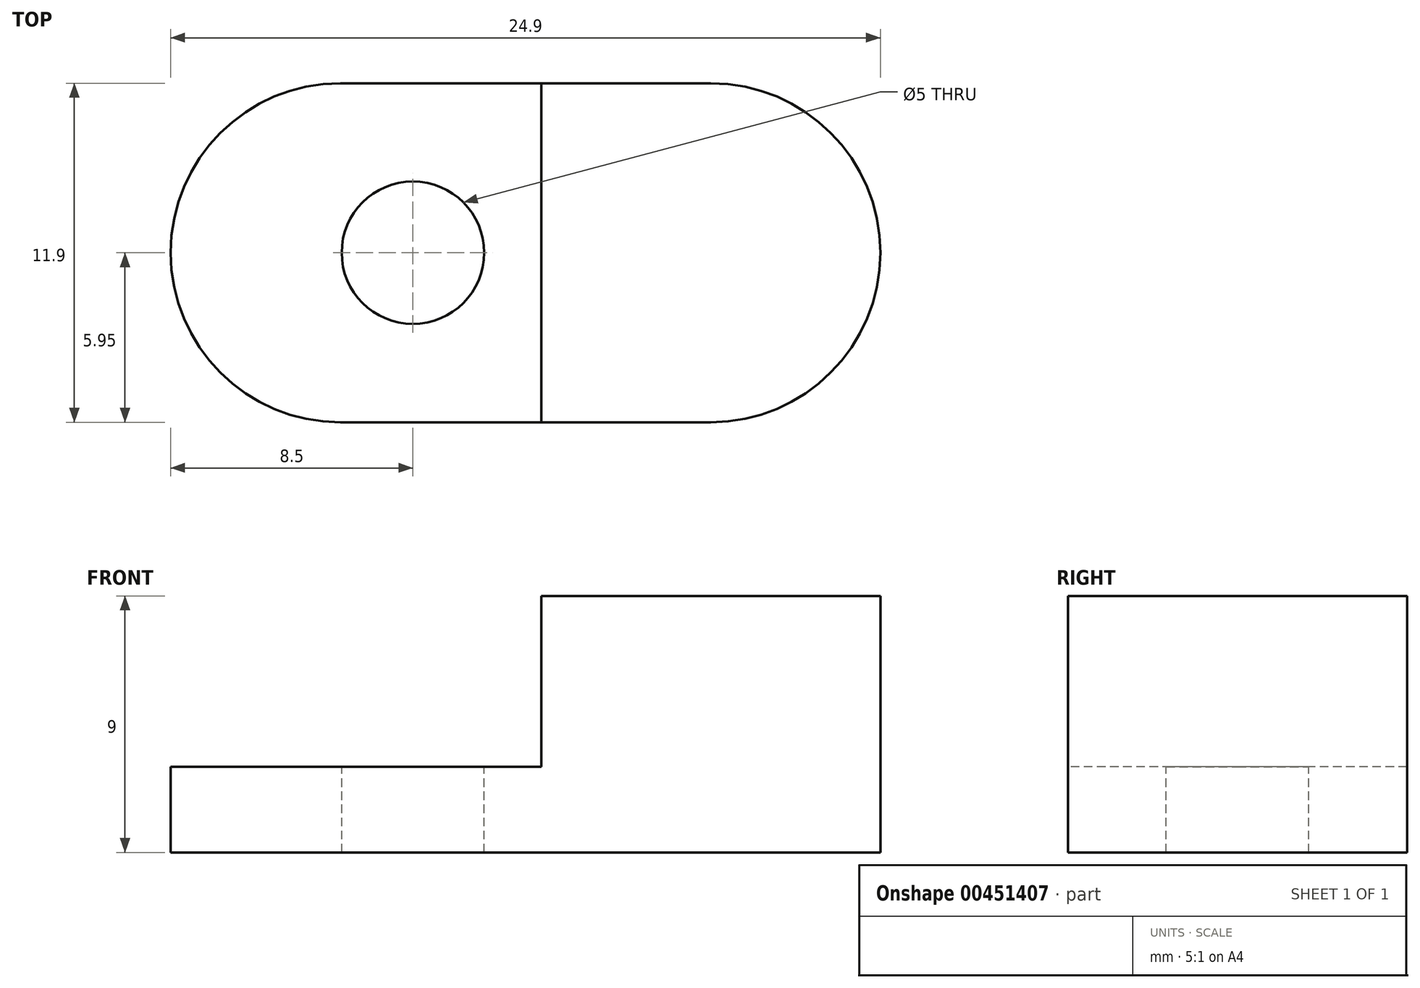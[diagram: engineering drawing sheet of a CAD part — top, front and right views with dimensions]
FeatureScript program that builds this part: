
annotation { "Feature Type Name" : "Feature", "Feature Type Description" : "" }
export const myFeature = defineFeature(function(context is Context, id is Id, definition is map)
    precondition{}
    {
        {
            var Q0;
            Q0=qCreatedBy(makeId("Top.planeOp"),FACE);
            var sketch = newSketch(context, id + "F0", { "sketchPlane" : qUnion([Q0])});
            skLineSegment(sketch, "E0.bottom", {"start": v(-6.5, -5.95) * mm, "end": v(6.5, -5.95) * mm});
            skLineSegment(sketch, "E0.top", {"start": v(-6.5, 5.95) * mm, "end": v(6.5, 5.95) * mm});
            skArc(sketch, "E1", {"start": v(-6.5, 5.95) * mm, "mid": v(-12.45, 0) * mm, "end": v(-6.5, -5.95) * mm});
            skLineSegment(sketch, "E2", {"start": v(-6.5, 8.48) * mm, "end": v(-6.5, -9.76) * mm, "construction": true});
            skArc(sketch, "E3.MirrorCS", {"start": v(6.5, 5.95) * mm, "mid": v(12.45, 0) * mm, "end": v(6.5, -5.95) * mm});
            skLineSegment(sketch, "E4", {"start": v(6.5, 7.97) * mm, "end": v(6.5, -10.02) * mm, "construction": true});
            skPoint(sketch, "E5.endSnap0", {"position": v(-12.45, 0) * mm});
            skCircle(sketch, "E6", {"center": v(-3.95, 0) * mm, "radius": 2.5 * mm});
            skLineSegment(sketch, "E7", {"start": v(-16.35, 0) * mm, "end": v(15.83, 0) * mm, "construction": true});
            skSolve(sketch);
        }
        {
            var Q0;
            Q0=makeQuery(id+"F0.imprint","IMPRINT",FACE,{"disambiguationData":[TD([[makeQuery(id+"F0.imprint","IMPRINT",EDGE,{"derivedFrom":sQuery(id+"F0.wireOp",EDGE,"E0.bottom")}),1.0]])]});
            var Q1;
            Q1=makeQuery(id+"F0.imprint","IMPRINT",FACE,{"disambiguationData":[TD([[makeQuery(id+"F0.imprint","IMPRINT",EDGE,{"derivedFrom":sQuery(id+"F0.wireOp",EDGE,"E6")}),1.0]])]});
            extrude(context, id + "F1", {"entities" : qUnion([Q0, Q1]), "depth" : 3 * mm});
        }
        {
            var Q0;
            Q0=makeQuery(id+"F1.opExtrude","CAP_FACE",FACE,{"disambiguationData":[OSD([sQuery(id+"F0.wireOp",EDGE,"E0.bottom"),sQuery(id+"F0.wireOp",EDGE,"E0.top"),sQuery(id+"F0.wireOp",EDGE,"E1"),sQuery(id+"F0.wireOp",EDGE,"E3.MirrorCS"),sQuery(id+"F0.wireOp",EDGE,"E6")])],"isStart":false});
            var sketch = newSketch(context, id + "F2", { "sketchPlane" : qUnion([Q0])});
            skLineSegment(sketch, "E8", {"start": v(0.55, 5.95) * mm, "end": v(0.55, -5.95) * mm});
            skPoint(sketch, "E8.endSnap0", {"position": v(0, -5.95) * mm});
            skLineSegment(sketch, "E9", {"start": v(0.55, -5.95) * mm, "end": v(6.5, -5.95) * mm});
            skArc(sketch, "E10", {"start": v(6.5, -5.95) * mm, "mid": v(12.45, 0) * mm, "end": v(6.5, 5.95) * mm});
            skLineSegment(sketch, "E11", {"start": v(0.55, 5.95) * mm, "end": v(6.5, 5.95) * mm});
            skSolve(sketch);
        }
        {
            var Q0;
            Q0=makeQuery(id+"F2.imprint","IMPRINT",FACE,{"disambiguationData":[TD([[makeQuery(id+"F2.imprint","IMPRINT",EDGE,{"derivedFrom":sQuery(id+"F2.wireOp",EDGE,"E8")}),1.0]])]});
            extrude(context, id + "F3", {"entities" : qUnion([Q0]), "operationType" : NewBodyOperationType.ADD, "depth" : 6 * mm});
        }
        {
            var Q0;
            Q0=makeQuery(id+"F1.opExtrude","CAP_FACE",FACE,{"disambiguationData":[OSD([sQuery(id+"F0.wireOp",EDGE,"E0.bottom"),sQuery(id+"F0.wireOp",EDGE,"E0.top"),sQuery(id+"F0.wireOp",EDGE,"E1"),sQuery(id+"F0.wireOp",EDGE,"E3.MirrorCS")])],"isStart":false});
            var sketch = newSketch(context, id + "F4", { "sketchPlane" : qUnion([Q0])});
            skPoint(sketch, "E12", {"position": v(-3.95, 0) * mm});
            skCircle(sketch, "E13", {"center": v(-3.95, 0) * mm, "radius": 2.5 * mm});
            skSolve(sketch);
        }
        {
            var Q0;
            Q0=makeQuery(id+"F4.imprint","IMPRINT",FACE,{"disambiguationData":[TD([[makeQuery(id+"F4.imprint","IMPRINT",EDGE,{"derivedFrom":sQuery(id+"F4.wireOp",EDGE,"E13")}),1.0]])]});
            extrude(context, id + "F5", {"entities" : qUnion([Q0]), "operationType" : NewBodyOperationType.REMOVE, "oppositeDirection" : true, "depth" : 3 * mm});
        }
    });
